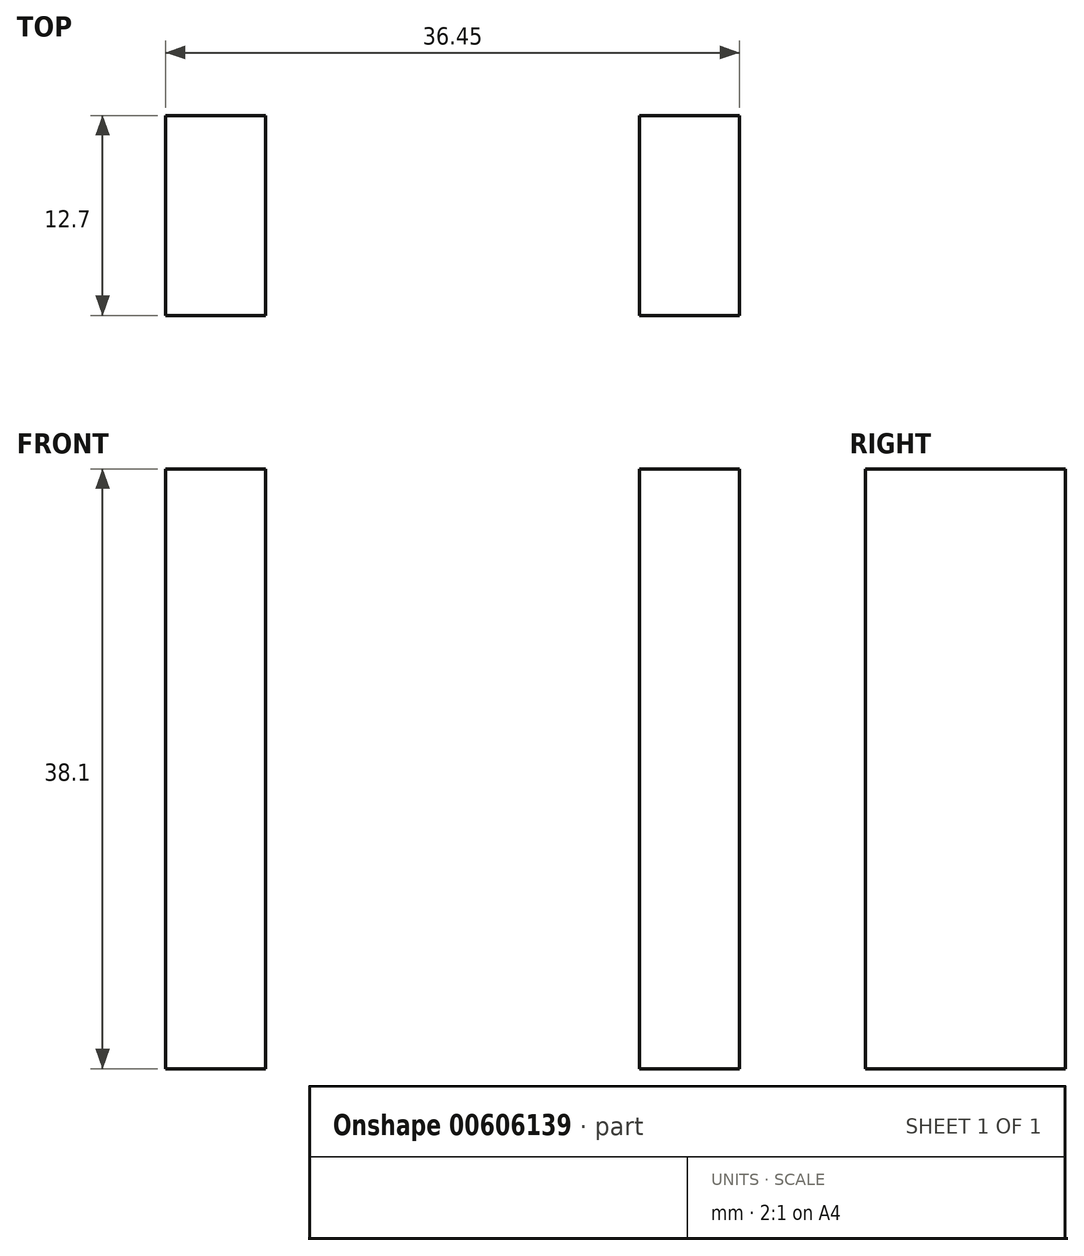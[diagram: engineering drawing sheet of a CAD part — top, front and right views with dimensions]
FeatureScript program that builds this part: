
annotation { "Feature Type Name" : "Feature", "Feature Type Description" : "" }
export const myFeature = defineFeature(function(context is Context, id is Id, definition is map)
    precondition{}
    {
        {
            var Q0;
            Q0=qCreatedBy(makeId("Front.planeOp"),FACE);
            var sketch = newSketch(context, id + "F0", { "sketchPlane" : qUnion([Q0])});
            skLineSegment(sketch, "E0.bottom", {"start": v(0, 0) * mm, "end": v(-6.35, 0) * mm});
            skLineSegment(sketch, "E0.top", {"start": v(0, 38.1) * mm, "end": v(-6.35, 38.1) * mm});
            skLineSegment(sketch, "E0.left", {"start": v(0, 0) * mm, "end": v(0, 38.1) * mm});
            skLineSegment(sketch, "E0.right", {"start": v(-6.35, 0) * mm, "end": v(-6.35, 38.1) * mm});
            skLineSegment(sketch, "E1", {"start": v(23.75, 0) * mm, "end": v(23.75, 38.1) * mm});
            skLineSegment(sketch, "E2", {"start": v(23.75, 38.1) * mm, "end": v(30.1, 38.1) * mm});
            skLineSegment(sketch, "E3", {"start": v(30.1, 38.1) * mm, "end": v(30.1, 0) * mm});
            skLineSegment(sketch, "E4", {"start": v(30.1, 0) * mm, "end": v(23.75, 0) * mm});
            skSolve(sketch);
        }
        {
            var Q0;
            Q0=makeQuery(id+"F0.imprint","IMPRINT",FACE,{"disambiguationData":[TD([[makeQuery(id+"F0.imprint","IMPRINT",EDGE,{"derivedFrom":sQuery(id+"F0.wireOp",EDGE,"E0.bottom")}),-1.0]])]});
            var Q1;
            Q1=makeQuery(id+"F0.imprint","IMPRINT",FACE,{"disambiguationData":[TD([[makeQuery(id+"F0.imprint","IMPRINT",EDGE,{"derivedFrom":sQuery(id+"F0.wireOp",EDGE,"E1")}),-1.0]])]});
            extrude(context, id + "F1", {"entities" : qUnion([Q0, Q1]), "depth" : 12.7 * mm, "offsetDistance" : 25.4 * mm});
        }
    });
